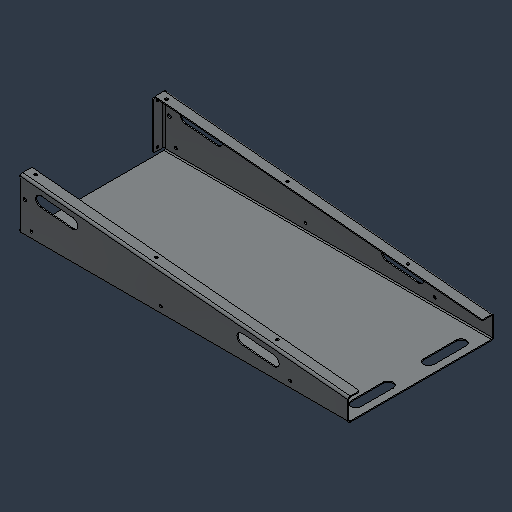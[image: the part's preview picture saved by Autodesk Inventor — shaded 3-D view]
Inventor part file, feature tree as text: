
AUTODESK INVENTOR PART (.ipt)
format: ipt  version: 2024.3 (Build 283343000, 343)  size: 185,856 bytes
history: native  units: mm (DEFAULTED — no unit token found)
features: fillet x1
ambient origin geometry x8: Origin, YZ Plane, XZ Plane, XY Plane, X Axis, Y Axis, Z Axis, Center Point
bodies: Solid1 (feature_tree)
feature tree (1):
  fillet  "Fillet3"  [1 undecoded]
note: 1 required parameter value undecoded (feature->parameter linkage not recoverable at this tier; creation-order binding heuristic only, values carry confidence <= 0.55)
